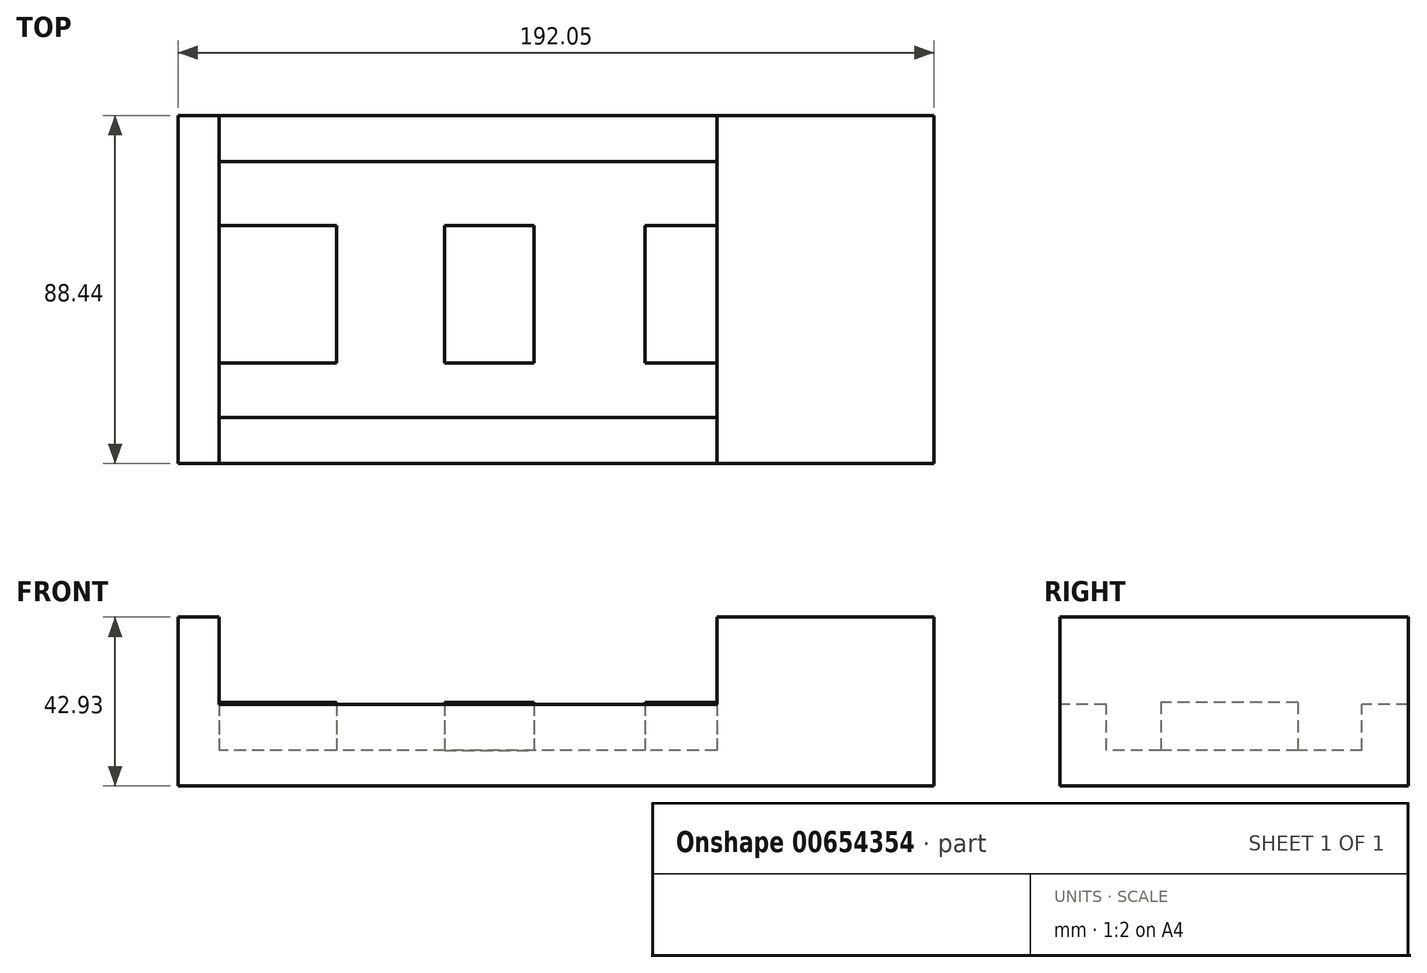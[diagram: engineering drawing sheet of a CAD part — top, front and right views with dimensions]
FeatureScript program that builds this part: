
annotation { "Feature Type Name" : "Feature", "Feature Type Description" : "" }
export const myFeature = defineFeature(function(context is Context, id is Id, definition is map)
    precondition{}
    {
        {
            var Q0;
            Q0=qCreatedBy(makeId("Top.planeOp"),FACE);
            var sketch = newSketch(context, id + "F0", { "sketchPlane" : qUnion([Q0])});
            skLineSegment(sketch, "E0.bottom", {"start": v(0, 0) * mm, "end": v(192.05, 0) * mm});
            skLineSegment(sketch, "E0.top", {"start": v(0, 88.44) * mm, "end": v(192.05, 88.44) * mm});
            skLineSegment(sketch, "E0.left", {"start": v(0, 0) * mm, "end": v(0, 88.44) * mm});
            skLineSegment(sketch, "E0.right", {"start": v(192.05, 0) * mm, "end": v(192.05, 88.44) * mm});
            skSolve(sketch);
        }
        {
            var Q0;
            Q0=makeQuery(id+"F0.imprint","IMPRINT",FACE,{"disambiguationData":[TD([[makeQuery(id+"F0.imprint","IMPRINT",EDGE,{"derivedFrom":sQuery(id+"F0.wireOp",EDGE,"E0.bottom")}),1.0]])]});
            extrude(context, id + "F1", {"entities" : qUnion([Q0]), "depth" : 42.93 * mm, "offsetDistance" : 25.4 * mm});
        }
        {
            var Q0;
            Q0=makeQuery(id+"F1.opExtrude","CAP_FACE",FACE,{"disambiguationData":[OSD([sQuery(id+"F0.wireOp",EDGE,"E0.bottom"),sQuery(id+"F0.wireOp",EDGE,"E0.top"),sQuery(id+"F0.wireOp",EDGE,"E0.left"),sQuery(id+"F0.wireOp",EDGE,"E0.right")])],"isStart":false});
            var sketch = newSketch(context, id + "F2", { "sketchPlane" : qUnion([Q0])});
            skLineSegment(sketch, "E1.bottom", {"start": v(136.88, 88.44) * mm, "end": v(10.36, 88.44) * mm});
            skLineSegment(sketch, "E1.top", {"start": v(136.88, 0) * mm, "end": v(10.36, 0) * mm});
            skLineSegment(sketch, "E1.left", {"start": v(136.88, 88.44) * mm, "end": v(136.88, 0) * mm});
            skLineSegment(sketch, "E1.right", {"start": v(10.36, 88.44) * mm, "end": v(10.36, 0) * mm});
            skSolve(sketch);
        }
        {
            var Q0;
            Q0=makeQuery(id+"F2.imprint","IMPRINT",FACE,{"disambiguationData":[TD([[makeQuery(id+"F2.imprint","IMPRINT",EDGE,{"derivedFrom":sQuery(id+"F2.wireOp",EDGE,"E1.bottom")}),-1.0]])]});
            extrude(context, id + "F3", {"entities" : qUnion([Q0]), "operationType" : NewBodyOperationType.REMOVE, "oppositeDirection" : true, "depth" : 22.15 * mm, "offsetDistance" : 25.4 * mm});
        }
        {
            var Q0;
            Q0=makeQuery(id+"F3.boolean.opBoolean","COPY",FACE,{"derivedFrom":makeQuery(id+"F3.opExtrude","CAP_FACE",FACE,{"disambiguationData":[OSD([sQuery(id+"F2.wireOp",EDGE,"E1.bottom"),sQuery(id+"F2.wireOp",EDGE,"E1.top"),sQuery(id+"F2.wireOp",EDGE,"E1.left"),sQuery(id+"F2.wireOp",EDGE,"E1.right")])],"isStart":false})});
            var sketch = newSketch(context, id + "F4", { "sketchPlane" : qUnion([Q0])});
            skLineSegment(sketch, "E2.bottom", {"start": v(136.88, 76.7) * mm, "end": v(10.36, 76.7) * mm});
            skLineSegment(sketch, "E2.top", {"start": v(136.88, 11.73) * mm, "end": v(10.36, 11.73) * mm});
            skLineSegment(sketch, "E2.left", {"start": v(136.88, 76.7) * mm, "end": v(136.88, 11.73) * mm});
            skLineSegment(sketch, "E2.right", {"start": v(10.36, 76.7) * mm, "end": v(10.36, 11.73) * mm});
            skSolve(sketch);
        }
        {
            var Q0;
            Q0=makeQuery(id+"F4.imprint","IMPRINT",FACE,{"disambiguationData":[TD([[makeQuery(id+"F4.imprint","IMPRINT",EDGE,{"derivedFrom":sQuery(id+"F4.wireOp",EDGE,"E2.bottom")}),1.0]])]});
            extrude(context, id + "F5", {"entities" : qUnion([Q0]), "operationType" : NewBodyOperationType.REMOVE, "oppositeDirection" : true, "depth" : 11.73 * mm, "offsetDistance" : 25.4 * mm});
        }
        {
            var Q0;
            Q0=makeQuery(id+"F5.boolean.opBoolean","COPY",FACE,{"derivedFrom":makeQuery(id+"F5.opExtrude","CAP_FACE",FACE,{"disambiguationData":[OSD([sQuery(id+"F4.wireOp",EDGE,"E2.bottom"),sQuery(id+"F4.wireOp",EDGE,"E2.top"),sQuery(id+"F4.wireOp",EDGE,"E2.left"),sQuery(id+"F4.wireOp",EDGE,"E2.right")])],"isStart":false})});
            var sketch = newSketch(context, id + "F6", { "sketchPlane" : qUnion([Q0])});
            skLineSegment(sketch, "E3.bottom", {"start": v(67.67, 60.48) * mm, "end": v(90.42, 60.48) * mm});
            skLineSegment(sketch, "E3.top", {"start": v(67.67, 25.58) * mm, "end": v(90.42, 25.58) * mm});
            skLineSegment(sketch, "E3.left", {"start": v(67.67, 60.48) * mm, "end": v(67.67, 25.58) * mm});
            skLineSegment(sketch, "E3.right", {"start": v(90.42, 60.48) * mm, "end": v(90.42, 25.58) * mm});
            skLineSegment(sketch, "E4.bottom", {"start": v(136.88, 60.48) * mm, "end": v(118.62, 60.48) * mm});
            skLineSegment(sketch, "E4.top", {"start": v(136.88, 25.58) * mm, "end": v(118.62, 25.58) * mm});
            skLineSegment(sketch, "E4.left", {"start": v(136.88, 60.48) * mm, "end": v(136.88, 25.58) * mm});
            skLineSegment(sketch, "E4.right", {"start": v(118.62, 60.48) * mm, "end": v(118.62, 25.58) * mm});
            skLineSegment(sketch, "E5.bottom", {"start": v(40.2, 60.48) * mm, "end": v(10.36, 60.48) * mm});
            skLineSegment(sketch, "E5.top", {"start": v(40.2, 25.58) * mm, "end": v(10.36, 25.58) * mm});
            skLineSegment(sketch, "E5.left", {"start": v(40.2, 60.48) * mm, "end": v(40.2, 25.58) * mm});
            skLineSegment(sketch, "E5.right", {"start": v(10.36, 60.48) * mm, "end": v(10.36, 25.58) * mm});
            skSolve(sketch);
        }
        {
            var Q0;
            Q0=makeQuery(id+"F6.imprint","IMPRINT",FACE,{"disambiguationData":[TD([[makeQuery(id+"F6.imprint","IMPRINT",EDGE,{"derivedFrom":sQuery(id+"F6.wireOp",EDGE,"E5.bottom")}),1.0]])]});
            var Q1;
            Q1=makeQuery(id+"F6.imprint","IMPRINT",FACE,{"disambiguationData":[TD([[makeQuery(id+"F6.imprint","IMPRINT",EDGE,{"derivedFrom":sQuery(id+"F6.wireOp",EDGE,"E3.bottom")}),-1.0]])]});
            var Q2;
            Q2=makeQuery(id+"F6.imprint","IMPRINT",FACE,{"disambiguationData":[TD([[makeQuery(id+"F6.imprint","IMPRINT",EDGE,{"derivedFrom":sQuery(id+"F6.wireOp",EDGE,"E4.bottom")}),1.0]])]});
            extrude(context, id + "F7", {"entities" : qUnion([Q0, Q1, Q2]), "operationType" : NewBodyOperationType.ADD, "depth" : 12.24 * mm, "offsetDistance" : 25.4 * mm});
        }
    });
